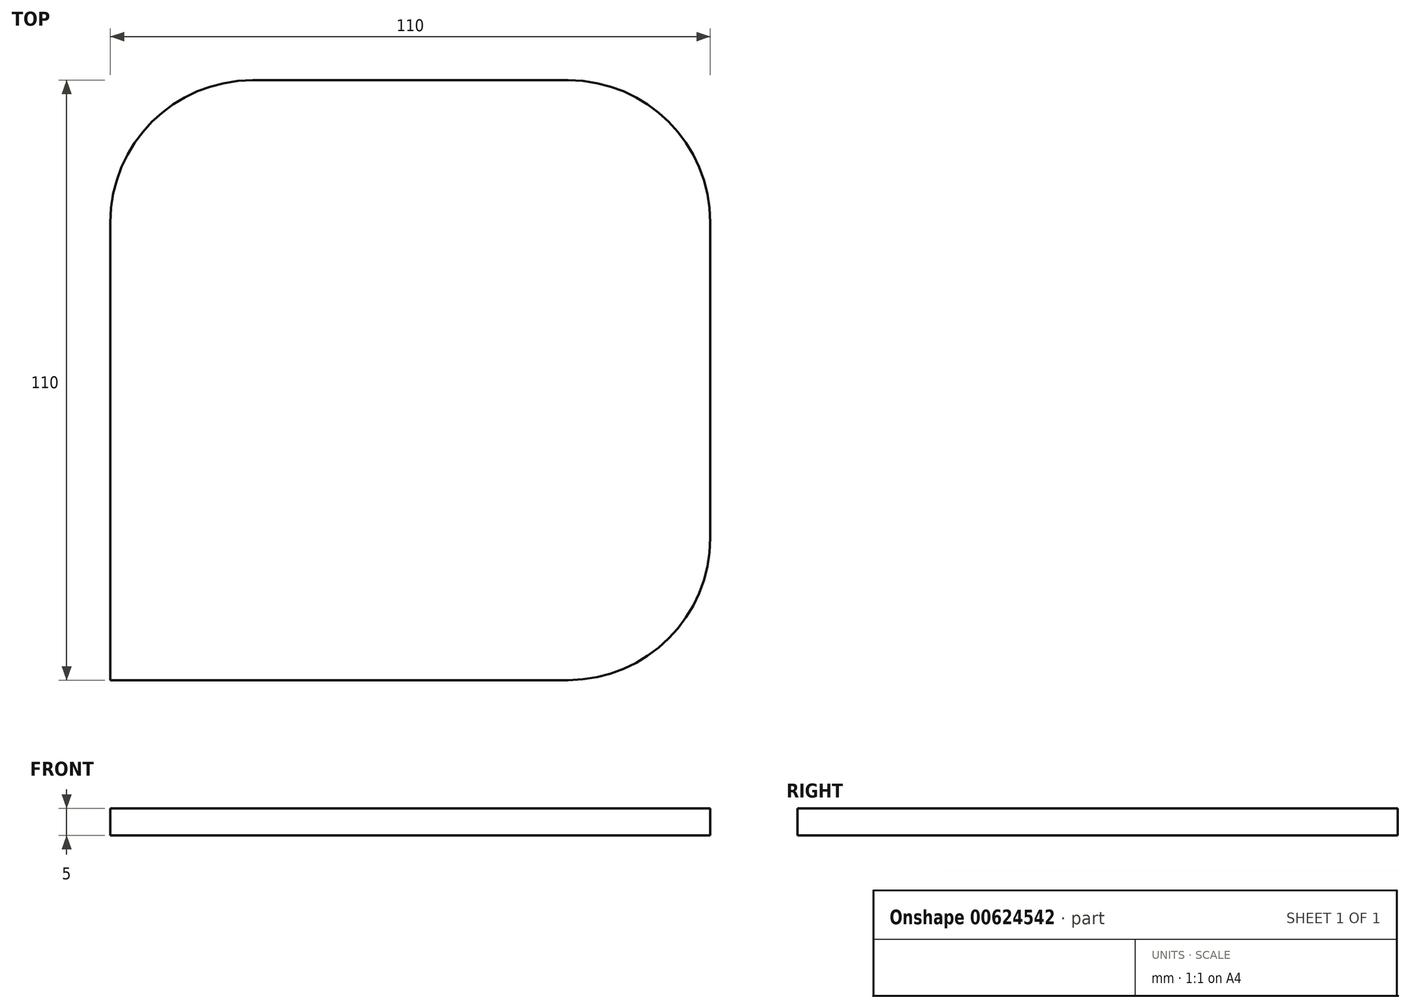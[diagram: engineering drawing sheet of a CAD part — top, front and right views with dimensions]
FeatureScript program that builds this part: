
annotation { "Feature Type Name" : "Feature", "Feature Type Description" : "" }
export const myFeature = defineFeature(function(context is Context, id is Id, definition is map)
    precondition{}
    {
        {
            var Q0;
            Q0=qCreatedBy(makeId("Top.planeOp"),FACE);
            var sketch = newSketch(context, id + "F0", { "sketchPlane" : qUnion([Q0])});
            skLineSegment(sketch, "E0.bottom", {"start": v(-57.68, 71.8) * mm, "end": v(52.32, 71.8) * mm});
            skLineSegment(sketch, "E0.top", {"start": v(-57.68, -38.2) * mm, "end": v(52.32, -38.2) * mm});
            skLineSegment(sketch, "E0.left", {"start": v(-57.68, 71.8) * mm, "end": v(-57.68, -38.2) * mm});
            skLineSegment(sketch, "E0.right", {"start": v(52.32, 71.8) * mm, "end": v(52.32, -38.2) * mm});
            skSolve(sketch);
        }
        {
            var Q0;
            Q0=makeQuery(id+"F0.imprint","IMPRINT",FACE,{"disambiguationData":[TD([[makeQuery(id+"F0.imprint","IMPRINT",EDGE,{"derivedFrom":sQuery(id+"F0.wireOp",EDGE,"E0.bottom")}),-1.0]])]});
            extrude(context, id + "F1", {"entities" : qUnion([Q0]), "depth" : 5 * mm, "offsetDistance" : 25 * mm});
        }
        {
            var Q0;
            Q0=makeQuery(id+"F1.opExtrude","SWEPT_EDGE",EDGE,{"disambiguationData":[OSD([sQuery(id+"F0.wireOp",EDGE,"E0.bottom"),sQuery(id+"F0.wireOp",EDGE,"E0.right")])]});
            var Q1;
            Q1=makeQuery(id+"F1.opExtrude","SWEPT_EDGE",EDGE,{"disambiguationData":[OSD([sQuery(id+"F0.wireOp",EDGE,"E0.bottom"),sQuery(id+"F0.wireOp",EDGE,"E0.left")])]});
            var Q2;
            Q2=makeQuery(id+"F1.opExtrude","SWEPT_EDGE",EDGE,{"disambiguationData":[OSD([sQuery(id+"F0.wireOp",EDGE,"E0.top"),sQuery(id+"F0.wireOp",EDGE,"E0.right")])]});
            fillet(context, id + "F2", {"entities" : qUnion([Q0, Q1, Q2]), "radius" : 26.07 * mm, "tangentPropagation" : true, "allowEdgeOverflow" : false});
        }
    });
